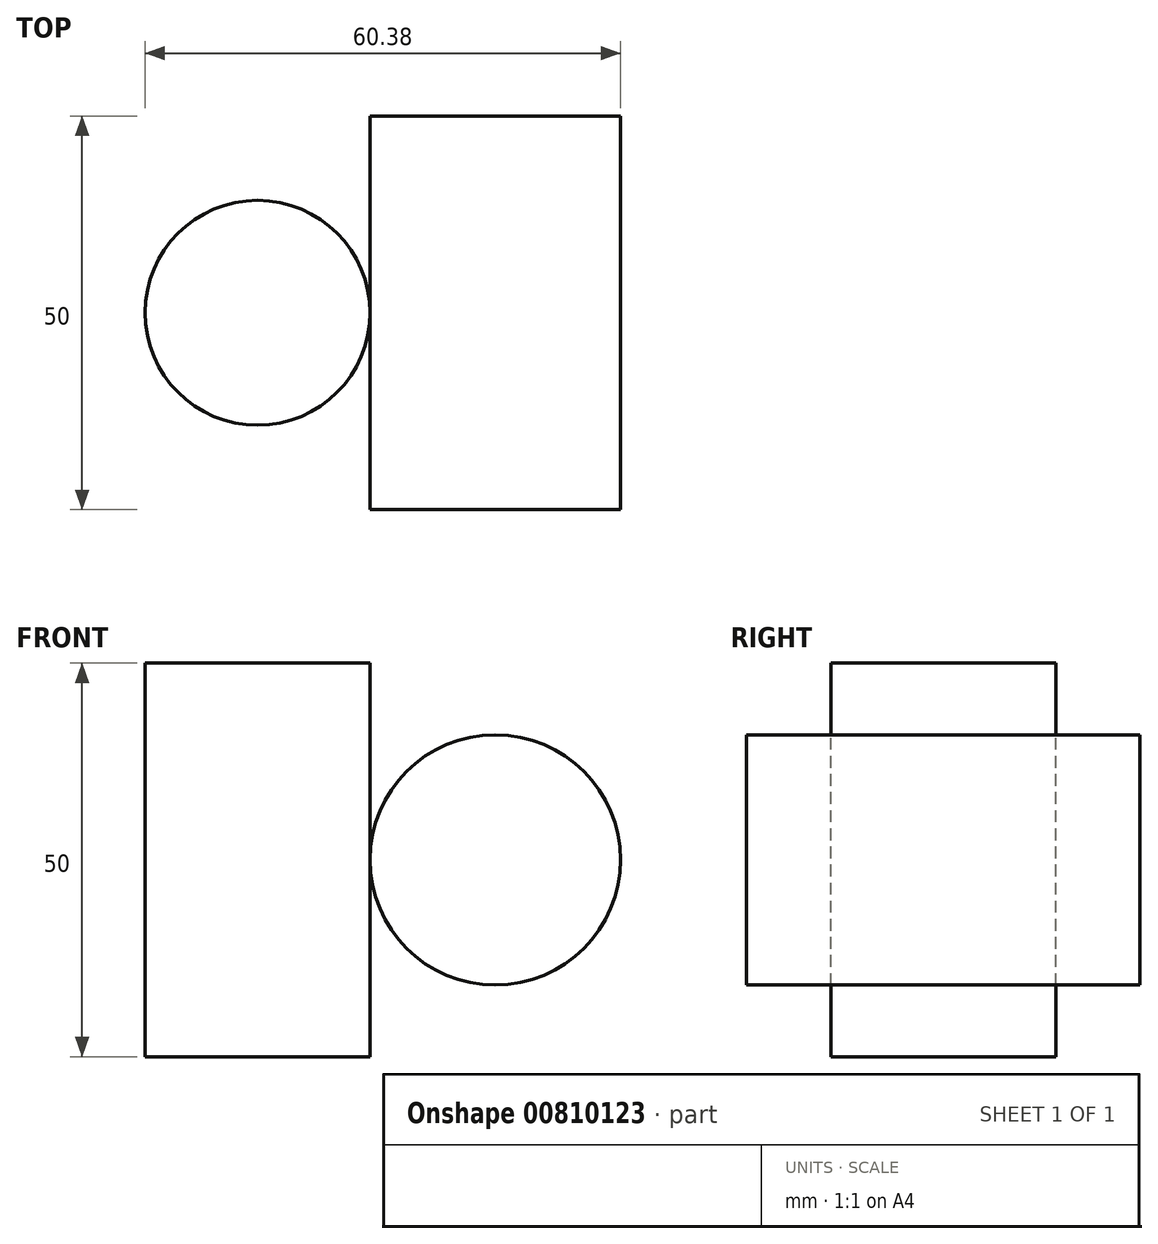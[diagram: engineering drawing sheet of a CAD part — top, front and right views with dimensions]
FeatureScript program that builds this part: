
annotation { "Feature Type Name" : "Feature", "Feature Type Description" : "" }
export const myFeature = defineFeature(function(context is Context, id is Id, definition is map)
    precondition{}
    {
        {
            var Q0;
            Q0=qCreatedBy(makeId("Top.planeOp"),FACE);
            var sketch = newSketch(context, id + "F0", { "sketchPlane" : qUnion([Q0])});
            skCircle(sketch, "E0", {"center": v(0, 0) * mm, "radius": 14.29 * mm});
            skSolve(sketch);
        }
        {
            var Q0;
            Q0 = qSketchRegion(id + "F0", true);
            var Q1;
            Q1=sQuery(id+"F0.wireOp",EDGE,"E0");
            extrude(context, id + "F1", {"entities" : qUnion([Q0]), "bodyType" : ToolBodyType.SURFACE, "surfaceEntities" : qUnion([Q1]), "endBound" : BoundingType.SYMMETRIC, "depth" : 50 * mm, "offsetDistance" : 25 * mm});
        }
        {
            var Q0;
            Q0=qCreatedBy(makeId("Front.planeOp"),FACE);
            var sketch = newSketch(context, id + "F2", { "sketchPlane" : qUnion([Q0])});
            skCircle(sketch, "E1", {"center": v(30.19, 0) * mm, "radius": 15.9 * mm});
            skLineSegment(sketch, "E2", {"start": v(0, 0) * mm, "end": v(30.19, 0) * mm});
            skSolve(sketch);
        }
        {
            var Q0;
            Q0=makeQuery(id+"F2.imprint","IMPRINT",FACE,{"disambiguationData":[TD([[makeQuery(id+"F2.imprint","IMPRINT",EDGE,{"derivedFrom":sQuery(id+"F2.wireOp",EDGE,"E1")}),1.0]])]});
            var Q1;
            Q1=sQuery(id+"F2.wireOp",EDGE,"E1");
            extrude(context, id + "F3", {"entities" : qUnion([Q0]), "bodyType" : ToolBodyType.SURFACE, "surfaceEntities" : qUnion([Q1]), "endBound" : BoundingType.SYMMETRIC, "depth" : 50 * mm, "offsetDistance" : 25 * mm});
        }
    });
